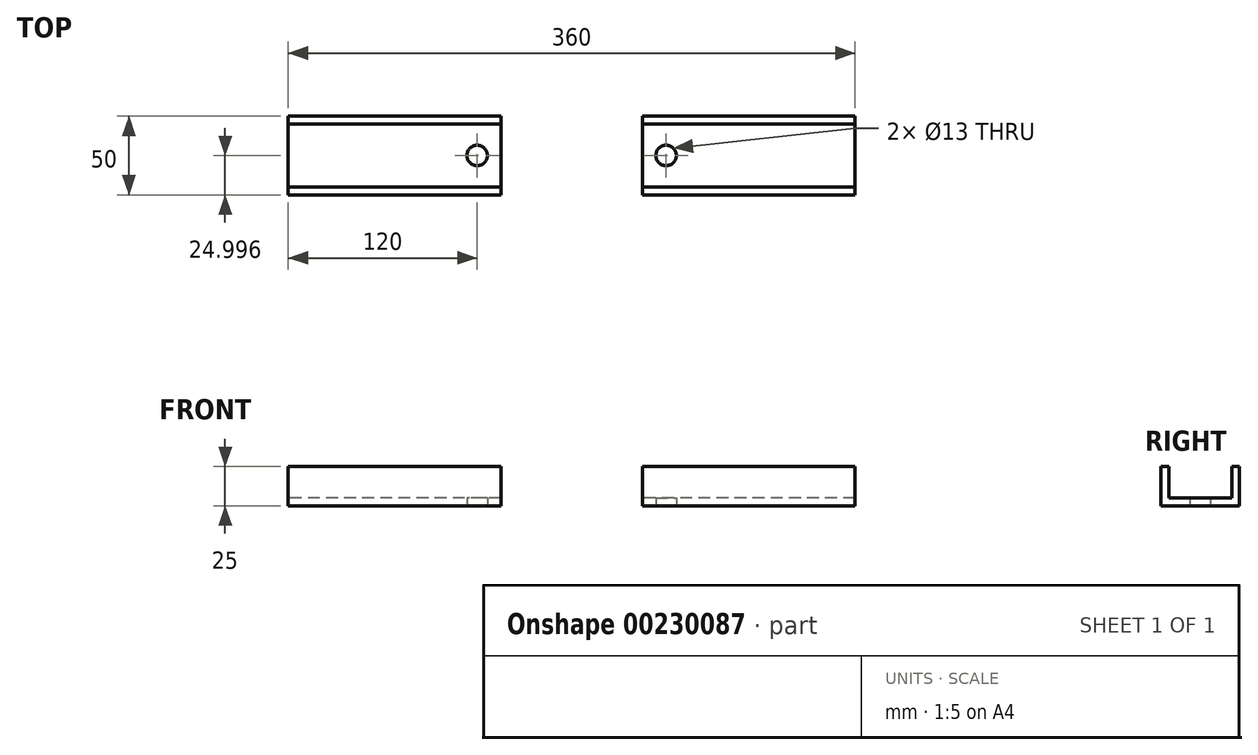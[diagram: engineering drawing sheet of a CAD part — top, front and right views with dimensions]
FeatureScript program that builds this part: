
annotation { "Feature Type Name" : "Feature", "Feature Type Description" : "" }
export const myFeature = defineFeature(function(context is Context, id is Id, definition is map)
    precondition{}
    {
        {
            var Q0;
            Q0=qCreatedBy(makeId("Right.planeOp"),FACE);
            var sketch = newSketch(context, id + "F0", { "sketchPlane" : qUnion([Q0])});
            skLineSegment(sketch, "E0.bottom", {"start": v(-16.15, 0) * mm, "end": v(-66.15, 0) * mm});
            skLineSegment(sketch, "E0.top", {"start": v(-16.15, 25) * mm, "end": v(-21.15, 25) * mm});
            skLineSegment(sketch, "E0.left", {"start": v(-16.15, 0) * mm, "end": v(-16.15, 25) * mm});
            skLineSegment(sketch, "E0.right", {"start": v(-66.15, 0) * mm, "end": v(-66.15, 25) * mm});
            skLineSegment(sketch, "E1.top", {"start": v(-61.15, 5) * mm, "end": v(-21.15, 5) * mm});
            skLineSegment(sketch, "E1.left", {"start": v(-61.15, 25) * mm, "end": v(-61.15, 5) * mm});
            skLineSegment(sketch, "E1.right", {"start": v(-21.15, 25) * mm, "end": v(-21.15, 5) * mm});
            skLineSegment(sketch, "E2.trimOffspring", {"start": v(-61.15, 25) * mm, "end": v(-66.15, 25) * mm});
            skSolve(sketch);
        }
        {
            var Q0;
            Q0 = qSketchRegion(id + "F0", true);
            extrude(context, id + "F1", {"entities" : qUnion([Q0]), "endBound" : BoundingType.SYMMETRIC, "depth" : 360 * mm});
        }
        {
            var Q0;
            Q0=makeQuery(id+"F1.opExtrude","SWEPT_FACE",FACE,{"disambiguationData":[OSD([sQuery(id+"F0.wireOp",EDGE,"E0.bottom")])]});
            var sketch = newSketch(context, id + "F2", { "sketchPlane" : qUnion([Q0])});
            skCircle(sketch, "E3", {"center": v(-60, 41.15) * mm, "radius": 6.5 * mm});
            skPoint(sketch, "E3.centerSnap0", {"position": v(-180, 41.15) * mm});
            skCircle(sketch, "E4", {"center": v(60, 41.15) * mm, "radius": 6.5 * mm});
            skPoint(sketch, "E4.centerSnap0", {"position": v(180, 41.15) * mm});
            skSolve(sketch);
        }
        {
            var Q0;
            Q0 = qSketchRegion(id + "F2", true);
            extrude(context, id + "F3", {"entities" : qUnion([Q0]), "operationType" : NewBodyOperationType.REMOVE, "oppositeDirection" : true, "depth" : 25 * mm});
        }
        {
            var Q0;
            Q0=makeQuery(id+"F1.opExtrude","SWEPT_FACE",FACE,{"disambiguationData":[OSD([sQuery(id+"F0.wireOp",EDGE,"E0.bottom")])]});
            var sketch = newSketch(context, id + "F4", { "sketchPlane" : qUnion([Q0])});
            skLineSegment(sketch, "E5.bottom", {"start": v(-45, 66.15) * mm, "end": v(45, 66.15) * mm});
            skLineSegment(sketch, "E5.top", {"start": v(-45, 16.15) * mm, "end": v(45, 16.15) * mm});
            skLineSegment(sketch, "E5.left", {"start": v(-45, 66.15) * mm, "end": v(-45, 16.15) * mm});
            skLineSegment(sketch, "E5.right", {"start": v(45, 66.15) * mm, "end": v(45, 16.15) * mm});
            skSolve(sketch);
        }
        {
            var Q0;
            Q0=makeQuery(id+"F4.imprint","IMPRINT",FACE,{"disambiguationData":[TD([[makeQuery(id+"F4.imprint","IMPRINT",EDGE,{"derivedFrom":sQuery(id+"F4.wireOp",EDGE,"E5.bottom")}),1.0]])]});
            extrude(context, id + "F5", {"entities" : qUnion([Q0]), "operationType" : NewBodyOperationType.REMOVE, "oppositeDirection" : true, "depth" : 25 * mm});
        }
    });
